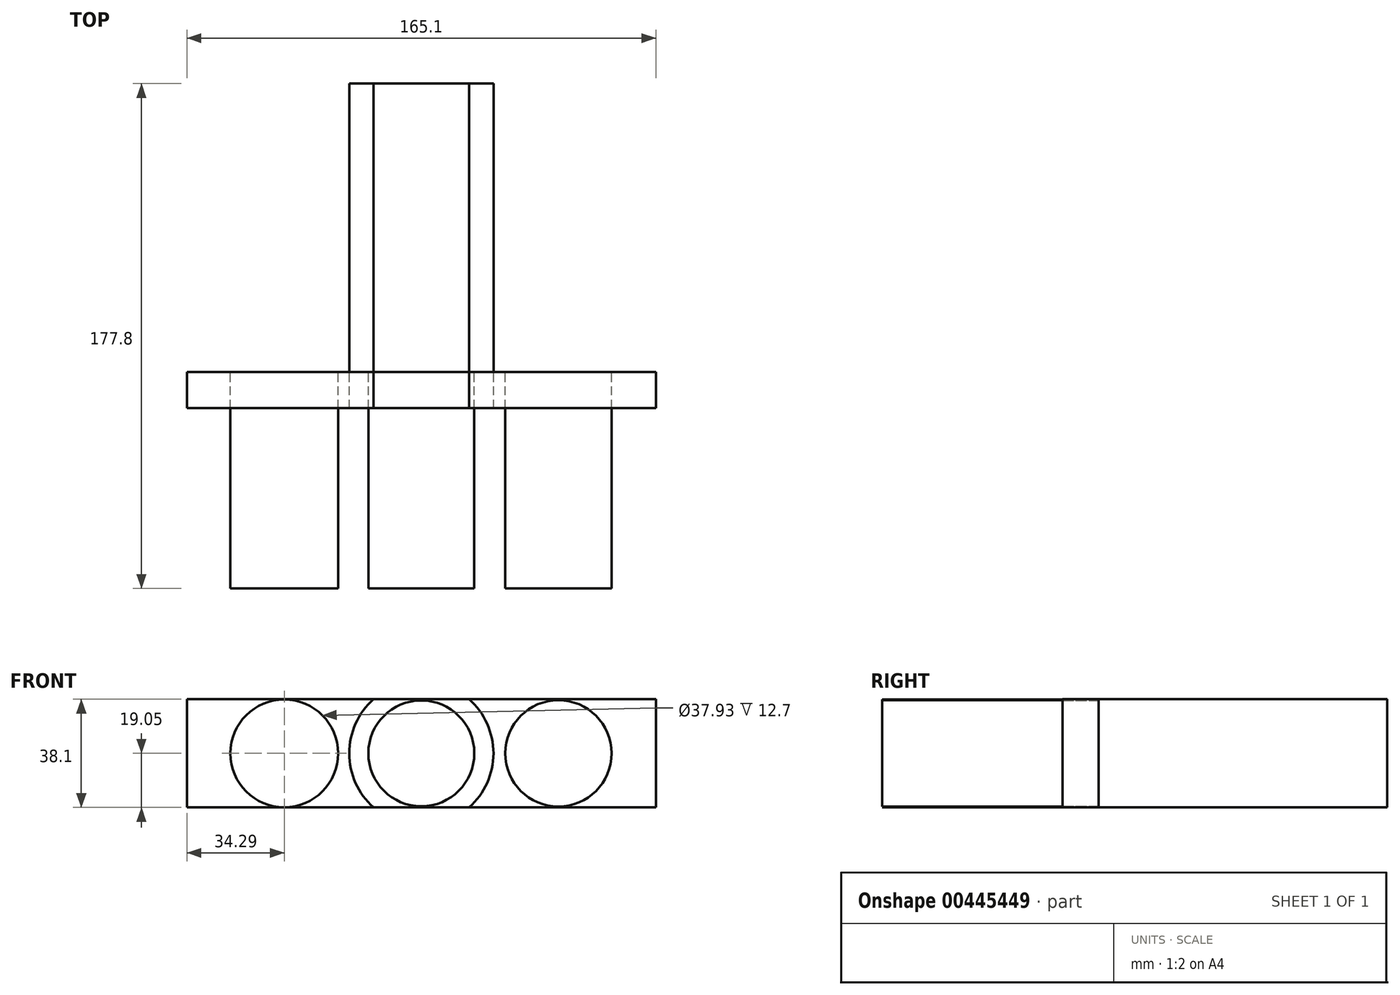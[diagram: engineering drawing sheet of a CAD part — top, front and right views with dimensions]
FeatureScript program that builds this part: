
annotation { "Feature Type Name" : "Feature", "Feature Type Description" : "" }
export const myFeature = defineFeature(function(context is Context, id is Id, definition is map)
    precondition{}
    {
        {
            var Q0;
            Q0=qCreatedBy(makeId("Front.planeOp"),FACE);
            var sketch = newSketch(context, id + "F0", { "sketchPlane" : qUnion([Q0])});
            skLineSegment(sketch, "E0.bottom", {"start": v(82.55, -19.05) * mm, "end": v(-82.55, -19.05) * mm});
            skLineSegment(sketch, "E0.top", {"start": v(82.55, 19.05) * mm, "end": v(-82.55, 19.05) * mm});
            skLineSegment(sketch, "E0.left", {"start": v(82.55, -19.05) * mm, "end": v(82.55, 19.05) * mm});
            skLineSegment(sketch, "E0.right", {"start": v(-82.55, -19.05) * mm, "end": v(-82.55, 19.05) * mm});
            skPoint(sketch, "E0.middle", {"position": v(0, 0) * mm});
            skCircle(sketch, "E1", {"center": v(-48.26, 0) * mm, "radius": 18.97 * mm});
            skCircle(sketch, "E2", {"center": v(48.26, 0) * mm, "radius": 18.73 * mm});
            skCircle(sketch, "E3", {"center": v(0, 0) * mm, "radius": 25.4 * mm});
            skCircle(sketch, "E4", {"center": v(0, 0) * mm, "radius": 18.65 * mm});
            skSolve(sketch);
        }
        {
            var Q0;
            Q0=makeQuery(id+"F0.imprint","IMPRINT",FACE,{"disambiguationData":[TD([[makeQuery(id+"F0.imprint","IMPRINT",EDGE,{"derivedFrom":sQuery(id+"F0.wireOp",EDGE,"E4")}),1.0]])]});
            var Q1;
            Q1=makeQuery(id+"F0.imprint","IMPRINT",FACE,{"disambiguationData":[TD([[makeQuery(id+"F0.imprint","IMPRINT",EDGE,{"derivedFrom":sQuery(id+"F0.wireOp",EDGE,"E1")}),1.0]])]});
            var Q2;
            Q2=makeQuery(id+"F0.imprint","IMPRINT",FACE,{"disambiguationData":[TD([[makeQuery(id+"F0.imprint","IMPRINT",EDGE,{"derivedFrom":sQuery(id+"F0.wireOp",EDGE,"E2")}),1.0]])]});
            extrude(context, id + "F1", {"entities" : qUnion([Q0, Q1, Q2]), "depth" : 76.2 * mm});
        }
        {
            var Q0;
            {var subQ0=sQuery(id+"F0.wireOp",EDGE,"E0.left");Q0=makeQuery(id+"F0.imprint","IMPRINT",FACE,{"disambiguationData":[TD([[makeQuery(id+"F0.imprint","IMPRINT",EDGE,{"derivedFrom":subQ0}),1.0]])]});}
            var Q1;
            {var subQ0=sQuery(id+"F0.wireOp",EDGE,"E0.right");Q1=makeQuery(id+"F0.imprint","IMPRINT",FACE,{"disambiguationData":[TD([[makeQuery(id+"F0.imprint","IMPRINT",EDGE,{"derivedFrom":subQ0}),-1.0]])]});}
            extrude(context, id + "F2", {"entities" : qUnion([Q0, Q1]), "depth" : 12.7 * mm});
        }
        {
            var Q0;
            Q0=makeQuery(id+"F0.imprint","IMPRINT",FACE,{"disambiguationData":[TD([[makeQuery(id+"F0.imprint","IMPRINT",EDGE,{"derivedFrom":sQuery(id+"F0.wireOp",EDGE,"E4")}),-1.0]])]});
            var Q1;
            Q1=makeQuery(id+"F0.imprint","IMPRINT",FACE,{"disambiguationData":[TD([[makeQuery(id+"F0.imprint","IMPRINT",EDGE,{"derivedFrom":sQuery(id+"F0.wireOp",EDGE,"E4")}),1.0]])]});
            var Q2;
            {var subQ0=sQuery(id+"F0.wireOp",EDGE,"E3");var subQ1=sQuery(id+"F0.wireOp",EDGE,"E0.bottom");var subQ2=makeQuery(id+"F0.imprint","INTERSECT",VERTEX,{"disambiguationData":[OD(0.0)],"derivedFrom":[subQ1,subQ0]});Q2=makeQuery(id+"F0.imprint","IMPRINT",FACE,{"disambiguationData":[TD([[makeQuery(id+"F0.imprint","IMPRINT",EDGE,{"disambiguationData":[TD([[subQ2,-1.0]])],"derivedFrom":subQ1}),1.0]])]});}
            var Q3;
            {var subQ0=sQuery(id+"F0.wireOp",EDGE,"E3");var subQ1=sQuery(id+"F0.wireOp",EDGE,"E0.top");var subQ2=makeQuery(id+"F0.imprint","INTERSECT",VERTEX,{"disambiguationData":[OD(0.0)],"derivedFrom":[subQ1,subQ0]});Q3=makeQuery(id+"F0.imprint","IMPRINT",FACE,{"disambiguationData":[TD([[makeQuery(id+"F0.imprint","IMPRINT",EDGE,{"disambiguationData":[TD([[subQ2,-1.0]])],"derivedFrom":subQ1}),-1.0]])]});}
            extrude(context, id + "F3", {"entities" : qUnion([Q0, Q1, Q2, Q3]), "operationType" : NewBodyOperationType.ADD, "oppositeDirection" : true, "depth" : 101.6 * mm});
        }
        {
            var Q0;
            Q0=makeQuery(id+"F0.imprint","IMPRINT",FACE,{"disambiguationData":[TD([[makeQuery(id+"F0.imprint","IMPRINT",EDGE,{"derivedFrom":sQuery(id+"F0.wireOp",EDGE,"E4")}),-1.0]])]});
            extrude(context, id + "F4", {"entities" : qUnion([Q0]), "depth" : 12.7 * mm});
        }
    });
